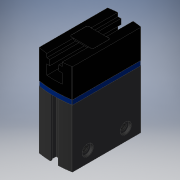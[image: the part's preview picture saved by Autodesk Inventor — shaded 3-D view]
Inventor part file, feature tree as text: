
AUTODESK INVENTOR PART (.ipt)
format: ipt  version: 2019 (Build 230136000, 136)  size: 339,968 bytes
history: native  units: mm
features: other x35, sketch x15, extrude x9, revolve x4, thread x4, hole x2
ambient origin geometry x8: Origin, YZ Plane, XZ Plane, XY Plane, X Axis, Y Axis, Z Axis, Center Point
bodies: Solid1 (feature_tree)
feature tree (69):
  extrude  "Extrusion1"  Depth=3.0mm TaperAngle=0.0deg
  extrude  "Extrusion2"  Depth=66.0mm TaperAngle=0.0deg
  extrude  "Extrusion3"  Depth=0.1mm TaperAngle=0.0deg
  extrude  "Extrusion4"  Depth=18.042mm TaperAngle=0.0deg
  extrude  "Extrusion5"  Depth=18.042mm TaperAngle=0.0deg
  extrude  "Extrusion6"  TaperAngle=360.0deg  [1 undecoded]
  revolve  "Revolution1"  Angle=360.0deg
  thread  "Thread1"  [1 undecoded]
  revolve  "Revolution2"  [1 undecoded]
  thread  "Thread2"  [1 undecoded]
  extrude  "Extrusion7"  TaperAngle=0.0deg  [1 undecoded]
  hole  "Hole1"  [1 undecoded]
  hole  "Hole2"  [1 undecoded]
  revolve  "Revolution3"  [1 undecoded]
  thread  "Thread3"  [1 undecoded]
  revolve  "Revolution4"  [1 undecoded]
  thread  "Thread4"  [1 undecoded]
  extrude  "Extrusion8"  [1 undecoded]
  extrude  "Extrusion9"  [1 undecoded]
  other  "GEHAEUSE_XY"
  other  "GEHAEUSE_YZ"
  other  "GEHAEUSE_ZX"
  other  "GEHAEUSE_X"
  other  "GEHAEUSE_Y"
  other  "GEHAEUSE_Z"
  other  "GEHAEUSE_Center"
  other  "TO_GREIF_XY"
  other  "TO_GREIF_YZ"
  other  "TO_GREIF_ZX"
  other  "TO_GREIF_X"
  other  "TO_GREIF_Y"
  other  "TO_GREIF_Z"
  other  "TO_GREIF_Center"
  other  "TO_GREIF_R_XY"
  other  "TO_GREIF_R_YZ"
  other  "TO_GREIF_R_ZX"
  other  "TO_GREIF_R_X"
  other  "TO_GREIF_R_Y"
  other  "TO_GREIF_R_Z"
  other  "TO_GREIF_R_Center"
  other  "TO_ZBH_1_XY"
  other  "TO_ZBH_1_YZ"
  other  "TO_ZBH_1_ZX"
  other  "TO_ZBH_1_X"
  other  "TO_ZBH_1_Y"
  other  "TO_ZBH_1_Z"
  other  "TO_ZBH_1_Center"
  other  "TO_ZBH_2_XY"
  other  "TO_ZBH_2_YZ"
  other  "TO_ZBH_2_ZX"
  other  "TO_ZBH_2_X"
  other  "TO_ZBH_2_Y"
  other  "TO_ZBH_2_Z"
  other  "TO_ZBH_2_Center"
  sketch  "Sketch_1"  dims[d0=38.1mm d1=0.0mm d2=3.0mm d3=0.0mm]
  sketch  "Sketch_2"  dims[d4=18.9mm d5=0.0mm d6=66.0mm d7=0.0mm]
  sketch  "Sketch_3"  dims[d8=0.8mm d9=0.0mm d10=0.1mm d11=0.0mm]
  sketch  "Sketch_4"  dims[d12=360.0deg d13=18.042mm d14=0.0mm]
  sketch  "Sketch_5"  dims[d15=360.0deg d16=18.042mm d17=0.0mm]
  sketch  "Sketch_15"
  sketch  "Sketch_6"  dims[d18=3.0mm d19=0.0mm]
  sketch  "Sketch_7"  dims[d20=2.459mm d21=6.0mm d22=3.0mm d23=2.0mm d24=90.0deg d25=7.0mm d26=0.0mm]
  sketch  "Sketch_8"  dims[d27=2.459mm d28=6.0mm d29=3.0mm d30=2.0mm d31=90.0deg d32=7.0mm d33=0.0mm d34=360.0deg]
  sketch  "Sketch10"  dims[d35=5.521mm d36=0.0mm d37=360.0deg d38=5.521mm d39=0.0mm]
  sketch  "Sketch11"  dims[d40=1.5mm d41=0.0mm d42=1.5mm d43=0.0mm d44=0.0mm]
  sketch  "Sketch_11"  dims[d45=0.0mm d46=0.0mm]
  sketch  "Sketch_12"
  sketch  "Sketch_17"
  sketch  "Sketch_18"
note: 13 required parameter values undecoded (feature->parameter linkage not recoverable at this tier; creation-order binding heuristic only, values carry confidence <= 0.55)